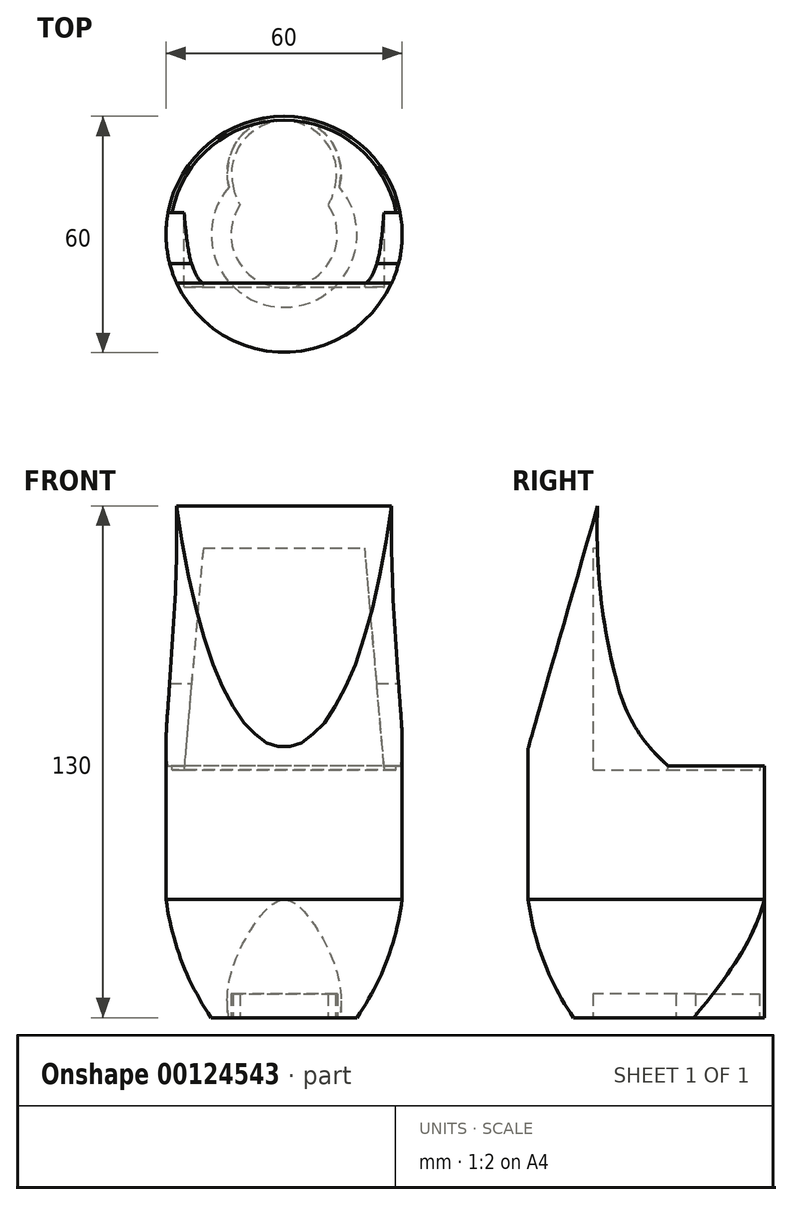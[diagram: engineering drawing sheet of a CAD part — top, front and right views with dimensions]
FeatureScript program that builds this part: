
annotation { "Feature Type Name" : "Feature", "Feature Type Description" : "" }
export const myFeature = defineFeature(function(context is Context, id is Id, definition is map)
    precondition{}
    {
        {
            var Q0;
            Q0=qCreatedBy(makeId("Top.planeOp"),FACE);
            var sketch = newSketch(context, id + "F0", { "sketchPlane" : qUnion([Q0])});
            skCircle(sketch, "E0", {"center": v(0, 0) * mm, "radius": 18.5 * mm});
            skSolve(sketch);
        }
        {
            var Q0;
            Q0=qCreatedBy(makeId("Front.planeOp"),FACE);
            var sketch = newSketch(context, id + "F1", { "sketchPlane" : qUnion([Q0])});
            skLineSegment(sketch, "E1", {"start": v(0, 0) * mm, "end": v(0, 150) * mm});
            skLineSegment(sketch, "E2", {"start": v(0, 0) * mm, "end": v(18.5, 0) * mm});
            skLineSegment(sketch, "E3", {"start": v(0, 30) * mm, "end": v(30, 30) * mm});
            skArc(sketch, "E4", {"start": v(18.5, 0) * mm, "mid": v(26.03, 14.32) * mm, "end": v(30, 30) * mm});
            skLineSegment(sketch, "E5", {"start": v(30, 30) * mm, "end": v(30, 150) * mm});
            skLineSegment(sketch, "E6", {"start": v(30, 150) * mm, "end": v(0, 150) * mm});
            skSolve(sketch);
        }
        {
            var Q0;
            {var subQ0=sQuery(id+"F1.wireOp",EDGE,"E2");Q0=makeQuery(id+"F1.imprint","IMPRINT",FACE,{"disambiguationData":[TD([[makeQuery(id+"F1.imprint","IMPRINT",EDGE,{"derivedFrom":subQ0}),1.0]])]});}
            var Q1;
            {var subQ2=sQuery(id+"F1.wireOp",EDGE,"E3");Q1=makeQuery(id+"F1.imprint","IMPRINT",FACE,{"disambiguationData":[TD([[makeQuery(id+"F1.imprint","IMPRINT",EDGE,{"derivedFrom":subQ2}),1.0]])]});}
            var Q2;
            Q2=sQuery(id+"F1.wireOp",EDGE,"E1");
            revolve(context, id + "F2", {"entities" : qUnion([Q0, Q1]), "axis" : qUnion([Q2]), "revolveType" : RevolveType.FULL});
        }
        {
            var Q0;
            Q0=makeQuery(id+"F0.imprint","IMPRINT",FACE,{"disambiguationData":[TD([[makeQuery(id+"F0.imprint","IMPRINT",EDGE,{"derivedFrom":sQuery(id+"F0.wireOp",EDGE,"E0")}),1.0]])]});
            var sketch = newSketch(context, id + "F3", { "sketchPlane" : qUnion([Q0])});
            skLineSegment(sketch, "E7", {"start": v(0, 12) * mm, "end": v(14, 12) * mm});
            skLineSegment(sketch, "E8", {"start": v(0, 12) * mm, "end": v(-14, 12) * mm});
            skArc(sketch, "E9", {"start": v(14, 12) * mm, "mid": v(0, 30) * mm, "end": v(-14, 12) * mm});
            skSolve(sketch);
        }
        {
            var Q0;
            {var subQ0=sQuery(id+"F3.wireOp",EDGE,"E9");var subQ1=makeQuery(id+"F0.imprint","IMPRINT",EDGE,{"derivedFrom":sQuery(id+"F0.wireOp",EDGE,"E0")});var subQ2=makeQuery(id+"F3.imprint","INTERSECT",VERTEX,{"disambiguationData":[OD(0.0)],"derivedFrom":[subQ1,subQ0]});Q0=makeQuery(id+"F3.imprint","IMPRINT",FACE,{"disambiguationData":[TD([[makeQuery(id+"F3.imprint","IMPRINT",EDGE,{"disambiguationData":[TD([[subQ2,-1.0]])],"derivedFrom":subQ0}),1.0]])]});}
            extrude(context, id + "F4", {"entities" : qUnion([Q0]), "operationType" : NewBodyOperationType.ADD, "endBound" : BoundingType.UP_TO_NEXT, "depth" : 25 * mm});
        }
        {
            var Q0;
            Q0=qCreatedBy(makeId("Right.planeOp"),FACE);
            var sketch = newSketch(context, id + "F5", { "sketchPlane" : qUnion([Q0])});
            skLineSegment(sketch, "E10", {"start": v(-31, 65) * mm, "end": v(-12.38, 130) * mm});
            skLineSegment(sketch, "E11", {"start": v(0, 173.2) * mm, "end": v(-45.06, 173.2) * mm});
            skLineSegment(sketch, "E12", {"start": v(-45.06, 173.2) * mm, "end": v(-45.06, 65) * mm});
            skLineSegment(sketch, "E13", {"start": v(-45.06, 65) * mm, "end": v(-31, 65) * mm});
            skLineSegment(sketch, "E14", {"start": v(0, 173.2) * mm, "end": v(33, 173.2) * mm});
            skLineSegment(sketch, "E15", {"start": v(33, 173.2) * mm, "end": v(33, 64) * mm});
            skLineSegment(sketch, "E16", {"start": v(33, 64) * mm, "end": v(5.57, 64) * mm});
            skArc(sketch, "E17", {"start": v(-12.38, 130) * mm, "mid": v(-11.43, 105.99) * mm, "end": v(-6.67, 82.43) * mm});
            skArc(sketch, "E18", {"start": v(-7.35, 84.9) * mm, "mid": v(-2.55, 73.42) * mm, "end": v(5.57, 64) * mm});
            skSolve(sketch);
        }
        {
            var Q0;
            Q0 = qSketchRegion(id + "F5", true);
            extrude(context, id + "F6", {"entities" : qUnion([Q0]), "operationType" : NewBodyOperationType.REMOVE, "endBound" : BoundingType.SYMMETRIC, "oppositeDirection" : true, "depth" : 60 * mm});
        }
        {
            var Q0;
            Q0=makeQuery(id+"F0.imprint","IMPRINT",FACE,{"disambiguationData":[TD([[makeQuery(id+"F0.imprint","IMPRINT",EDGE,{"derivedFrom":sQuery(id+"F0.wireOp",EDGE,"E0")}),1.0]])]});
            var sketch = newSketch(context, id + "F7", { "sketchPlane" : qUnion([Q0])});
            skArc(sketch, "E19", {"start": v(-11.2, 7.54) * mm, "mid": v(0, -13.5) * mm, "end": v(11.2, 7.54) * mm});
            skArc(sketch, "E20", {"start": v(13.02, 12.53) * mm, "mid": v(0, 28.8) * mm, "end": v(-13.02, 12.53) * mm});
            skArc(sketch, "E21", {"start": v(11.2, 7.54) * mm, "mid": v(12.36, 9.94) * mm, "end": v(13.02, 12.53) * mm});
            skArc(sketch, "E22.MirrorCS", {"start": v(-11.2, 7.54) * mm, "mid": v(-12.36, 9.94) * mm, "end": v(-13.02, 12.53) * mm});
            skSolve(sketch);
        }
        {
            var Q0;
            Q0 = qSketchRegion(id + "F7", true);
            extrude(context, id + "F8", {"entities" : qUnion([Q0]), "operationType" : NewBodyOperationType.REMOVE, "depth" : 6 * mm});
        }
        {
            var Q0;
            Q0=makeQuery(id+"F6.boolean.opBoolean","COPY",FACE,{"derivedFrom":makeQuery(id+"F6.opExtrude","SWEPT_FACE",FACE,{"disambiguationData":[OSD([sQuery(id+"F5.wireOp",EDGE,"E16")])]})});
            var sketch = newSketch(context, id + "F9", { "sketchPlane" : qUnion([Q0])});
            skArc(sketch, "E23", {"start": v(28.48, 5.57) * mm, "mid": v(0, 29.03) * mm, "end": v(-28.48, 5.57) * mm});
            skLineSegment(sketch, "E24", {"start": v(28.48, 5.57) * mm, "end": v(-28.48, 5.57) * mm});
            skSolve(sketch);
        }
        {
            var Q0;
            Q0=makeQuery(id+"F9.imprint","IMPRINT",FACE,{"disambiguationData":[TD([[makeQuery(id+"F9.imprint","IMPRINT",EDGE,{"derivedFrom":sQuery(id+"F9.wireOp",EDGE,"E23")}),1.0]])]});
            extrude(context, id + "F10", {"entities" : qUnion([Q0]), "operationType" : NewBodyOperationType.REMOVE, "oppositeDirection" : true, "depth" : 1 * mm});
        }
        {
            var Q0;
            Q0=makeQuery(id+"F10.boolean.opBoolean","COPY",FACE,{"derivedFrom":makeQuery(id+"F10.opExtrude","SWEPT_FACE",FACE,{"disambiguationData":[OSD([sQuery(id+"F9.wireOp",EDGE,"E24")])]})});
            var sketch = newSketch(context, id + "F11", { "sketchPlane" : qUnion([Q0])});
            skLineSegment(sketch, "E25", {"start": v(25.46, 63) * mm, "end": v(-25.46, 63) * mm});
            skLineSegment(sketch, "E26", {"start": v(-25.46, 63) * mm, "end": v(-19.77, 128) * mm});
            skLineSegment(sketch, "E27", {"start": v(-19.77, 128) * mm, "end": v(19.77, 128) * mm});
            skLineSegment(sketch, "E28", {"start": v(19.77, 128) * mm, "end": v(25.46, 63) * mm});
            skSolve(sketch);
        }
        {
            var Q0;
            Q0 = qSketchRegion(id + "F11", true);
            var Q1;
            {var subQ0=sQuery(id+"F11.wireOp",EDGE,"E27");Q1=makeQuery(id+"F11.imprint","IMPRINT",FACE,{"disambiguationData":[TD([[makeQuery(id+"F11.imprint","IMPRINT",EDGE,{"derivedFrom":subQ0}),-1.0]])]});}
            extrude(context, id + "F12", {"entities" : qUnion([Q0, Q1]), "operationType" : NewBodyOperationType.REMOVE, "oppositeDirection" : true, "depth" : 18 * mm});
        }
        {
            var Q0;
            Q0=makeQuery(id+"F12.boolean.opBoolean","COPY",FACE,{"derivedFrom":makeQuery(id+"F12.opExtrude","CAP_FACE",FACE,{"disambiguationData":[OSD([sQuery(id+"F11.wireOp",EDGE,"E25"),sQuery(id+"F11.wireOp",EDGE,"E26"),sQuery(id+"F11.wireOp",EDGE,"E27"),sQuery(id+"F11.wireOp",EDGE,"E28")])],"isStart":false})});
            extrude(context, id + "F13", {"entities" : qUnion([Q0]), "operationType" : NewBodyOperationType.REMOVE, "oppositeDirection" : true, "depth" : 1 * mm});
        }
    });
